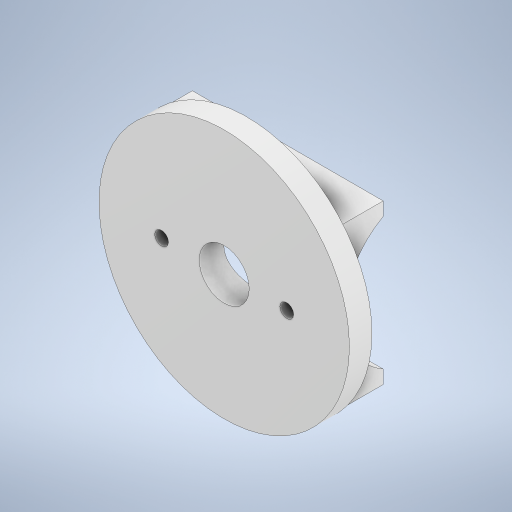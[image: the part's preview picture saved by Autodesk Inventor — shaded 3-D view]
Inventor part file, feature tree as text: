
AUTODESK INVENTOR PART (.ipt)
format: ipt  version: 2023 (Build 270158030, 158C)  size: 262,656 bytes
history: native  units: in
note: dims shown in document units (in); Inventor stores cm internally (conversion verified against a paired STEP export)
features: sketch x4, extrude x3, hole x1
ambient origin geometry x8: Origin, YZ Plane, XZ Plane, XY Plane, X Axis, Y Axis, Z Axis, Center Point
bodies: Solid1 (feature_tree)
feature tree (8):
  extrude  "Extrusion1"  Depth=2.5in
  extrude  "Extrusion2"  Depth=1.0in
  extrude  "Extrusion3"  Depth=3.937in
  hole  "Hole1"  [1 undecoded]
  sketch  "Sketch1"  dims[d1=2.375in d3=2.5in]
  sketch  "Sketch2"  dims[d4=1.5748in d5=1.0in]
  sketch  "Sketch3"  dims[d6=3.0in d7=0.0in d8=3.937in]
  sketch  "Sketch5"  dims[d9=0.3543in d10=0.0in d11=0.7874in d12=0.0in d13=0.0in d14=0.2165in d15=0.3389in d16=0.0246in d17=0.426in d18=0.5906in d19=0.1693in d20=90.0deg d21=0.3543in d22=0.8108in d23=1.9685in d24=0.0394in d25=0.0394in d26=0.0394in d27=0.0059in d28=0.0098in d29=0.0148in d30=0.5635in d31=0.0295in d32=0.8108in d33=0.0025in d34=0.0295in d35=0.0148in]
note: 1 required parameter value undecoded (feature->parameter linkage not recoverable at this tier; creation-order binding heuristic only, values carry confidence <= 0.55)
